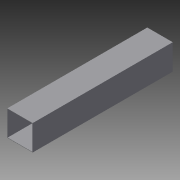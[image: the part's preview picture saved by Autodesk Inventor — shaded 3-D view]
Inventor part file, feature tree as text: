
AUTODESK INVENTOR PART (.ipt)
format: ipt  version: 2015 SP1 (Build 190203100, 203)  size: 106,496 bytes
history: native  units: in
note: dims shown in document units (in); Inventor stores cm internally (conversion verified against a paired STEP export)
features: sketch x4, extrude x3
ambient origin geometry x8: Origin, YZ Plane, XZ Plane, XY Plane, X Axis, Y Axis, Z Axis, Center Point
bodies: Solid1 (feature_tree)
feature tree (7):
  extrude  "Extrusion1"  Depth=2.0in
  extrude  "Extrusion2"  Depth=11.0in TaperAngle=0.0deg
  sketch  "Sketch3"  dims[d5=2.0in d6=0.03in]
  extrude  "Extrusion3"  Depth=0.03in
  sketch  "Sketch1"  dims[d0=2.0in d1=2.0in]
  sketch  "Sketch2"  dims[d2=0.03in d3=11.0in d4=0.0in]
  sketch  "Sketch4"  dims[d7=3.5in d8=0.0in d9=2.0in d10=0.03in d11=7.0in d12=0.0in]
